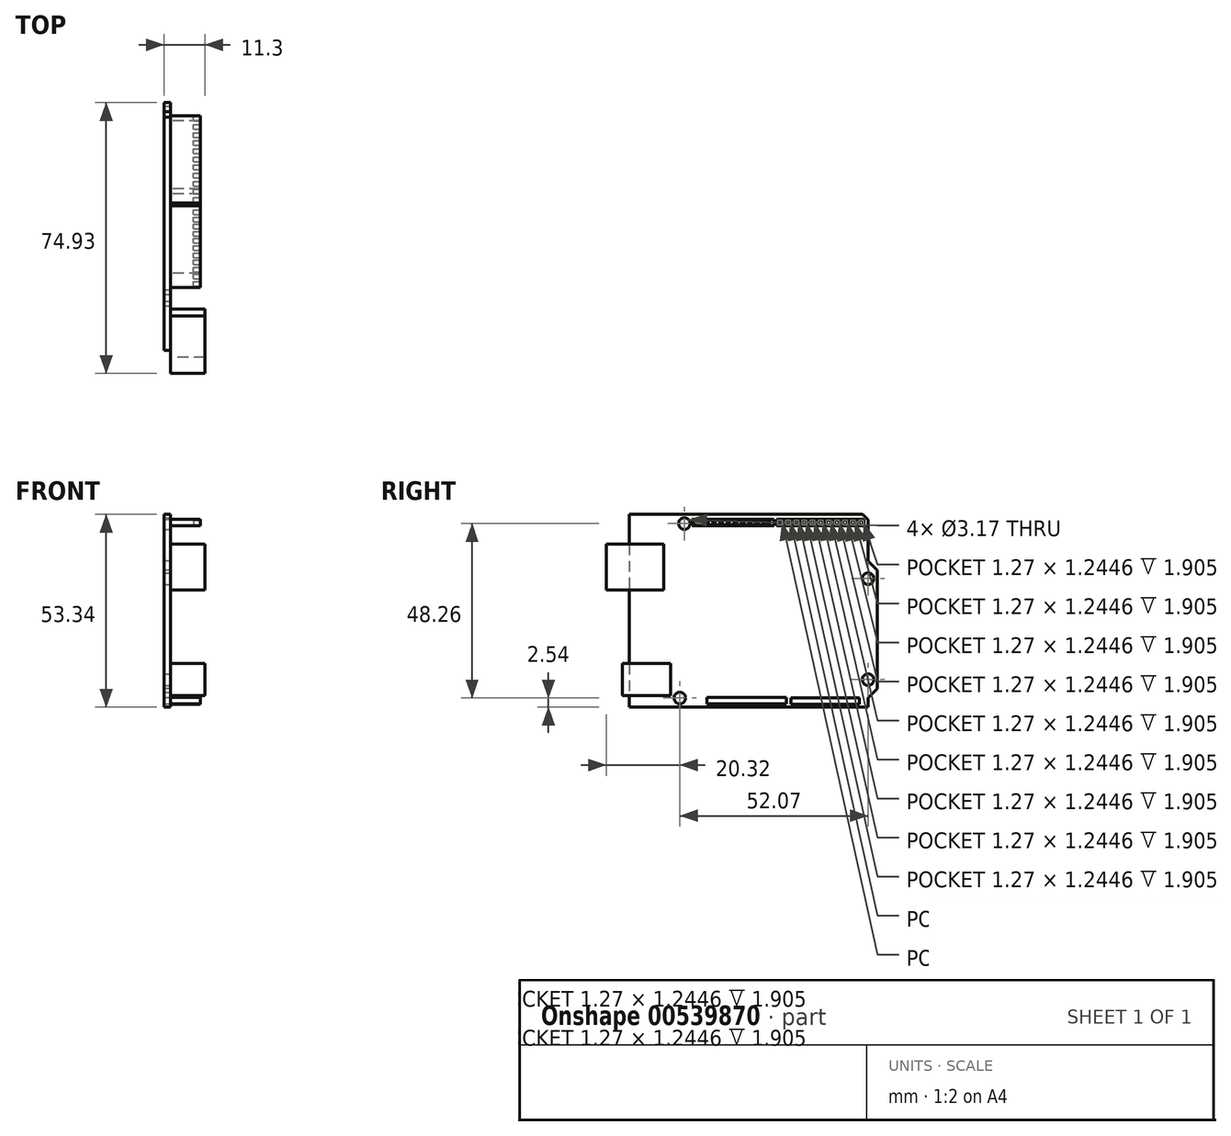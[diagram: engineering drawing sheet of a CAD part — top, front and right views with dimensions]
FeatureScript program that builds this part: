
annotation { "Feature Type Name" : "Feature", "Feature Type Description" : "" }
export const myFeature = defineFeature(function(context is Context, id is Id, definition is map)
    precondition{}
    {
        {
            var Q0;
            Q0=qCreatedBy(makeId("Right.planeOp"),FACE);
            var sketch = newSketch(context, id + "F0", { "sketchPlane" : qUnion([Q0])});
            skPoint(sketch, "E0", {"position": v(0, 53.34) * mm});
            skPoint(sketch, "E1", {"position": v(64.52, 53.34) * mm});
            skPoint(sketch, "E2", {"position": v(66.04, 0) * mm});
            skPoint(sketch, "E3", {"position": v(66.04, 2.54) * mm});
            skPoint(sketch, "E4", {"position": v(68.58, 5.08) * mm});
            skPoint(sketch, "E5", {"position": v(68.58, 37.85) * mm});
            skPoint(sketch, "E6", {"position": v(66.04, 40.39) * mm});
            skPoint(sketch, "E7", {"position": v(66.04, 51.82) * mm});
            skLineSegment(sketch, "E8", {"start": v(0, 53.34) * mm, "end": v(0, 0) * mm});
            skLineSegment(sketch, "E9", {"start": v(0, 0) * mm, "end": v(66.04, 0) * mm});
            skLineSegment(sketch, "E10", {"start": v(66.04, 2.54) * mm, "end": v(68.58, 5.08) * mm});
            skLineSegment(sketch, "E11", {"start": v(68.58, 37.85) * mm, "end": v(66.04, 40.39) * mm});
            skLineSegment(sketch, "E12", {"start": v(66.04, 51.82) * mm, "end": v(64.52, 53.34) * mm});
            skLineSegment(sketch, "E13", {"start": v(66.04, 2.54) * mm, "end": v(66.04, 0) * mm});
            skLineSegment(sketch, "E14", {"start": v(68.58, 5.08) * mm, "end": v(68.58, 37.85) * mm});
            skLineSegment(sketch, "E15", {"start": v(66.04, 40.39) * mm, "end": v(66.04, 51.82) * mm});
            skLineSegment(sketch, "E16", {"start": v(0, 53.34) * mm, "end": v(64.52, 53.34) * mm});
            skSolve(sketch);
        }
        {
            var Q0;
            Q0 = qSketchRegion(id + "F0", true);
            extrude(context, id + "F1", {"entities" : qUnion([Q0]), "depth" : 1.78 * mm, "offsetDistance" : 25.4 * mm});
        }
        {
            var Q0;
            Q0=makeQuery(id+"F1.opExtrude","CAP_FACE",FACE,{"disambiguationData":[OSD([sQuery(id+"F0.wireOp",EDGE,"E10"),sQuery(id+"F0.wireOp",EDGE,"E11"),sQuery(id+"F0.wireOp",EDGE,"E12"),sQuery(id+"F0.wireOp",EDGE,"E9"),sQuery(id+"F0.wireOp",EDGE,"E13"),sQuery(id+"F0.wireOp",EDGE,"E14"),sQuery(id+"F0.wireOp",EDGE,"E15"),sQuery(id+"F0.wireOp",EDGE,"E16"),sQuery(id+"F0.wireOp",EDGE,"E8")])],"isStart":false});
            var sketch = newSketch(context, id + "F2", { "sketchPlane" : qUnion([Q0])});
            skCircle(sketch, "E17", {"center": v(13.97, 2.54) * mm, "radius": 1.59 * mm});
            skCircle(sketch, "E18", {"center": v(15.24, 50.8) * mm, "radius": 1.59 * mm});
            skCircle(sketch, "E19", {"center": v(66.04, 35.56) * mm, "radius": 1.59 * mm});
            skCircle(sketch, "E20", {"center": v(66.04, 7.62) * mm, "radius": 1.59 * mm});
            skSolve(sketch);
        }
        {
            var Q0;
            Q0 = qSketchRegion(id + "F2", true);
            extrude(context, id + "F3", {"entities" : qUnion([Q0]), "operationType" : NewBodyOperationType.REMOVE, "oppositeDirection" : true, "depth" : 1.78 * mm, "offsetDistance" : 25.4 * mm});
        }
        {
            var Q0;
            Q0=makeQuery(id+"F1.opExtrude","CAP_FACE",FACE,{"disambiguationData":[OSD([sQuery(id+"F0.wireOp",EDGE,"E10"),sQuery(id+"F0.wireOp",EDGE,"E11"),sQuery(id+"F0.wireOp",EDGE,"E12"),sQuery(id+"F0.wireOp",EDGE,"E9"),sQuery(id+"F0.wireOp",EDGE,"E13"),sQuery(id+"F0.wireOp",EDGE,"E14"),sQuery(id+"F0.wireOp",EDGE,"E15"),sQuery(id+"F0.wireOp",EDGE,"E16"),sQuery(id+"F0.wireOp",EDGE,"E8")])],"isStart":false});
            var sketch = newSketch(context, id + "F4", { "sketchPlane" : qUnion([Q0])});
            skLineSegment(sketch, "E21.bottom", {"start": v(-1.9, 12.07) * mm, "end": v(11.43, 12.07) * mm});
            skLineSegment(sketch, "E21.top", {"start": v(-1.9, 3.18) * mm, "end": v(11.43, 3.18) * mm});
            skLineSegment(sketch, "E21.left", {"start": v(-1.9, 12.06) * mm, "end": v(-1.9, 3.17) * mm});
            skLineSegment(sketch, "E21.right", {"start": v(11.43, 12.07) * mm, "end": v(11.43, 3.18) * mm});
            skLineSegment(sketch, "E22.bottom", {"start": v(-6.35, 45.09) * mm, "end": v(9.53, 45.09) * mm});
            skLineSegment(sketch, "E22.top", {"start": v(-6.35, 32.39) * mm, "end": v(9.53, 32.39) * mm});
            skLineSegment(sketch, "E22.left", {"start": v(-6.35, 45.09) * mm, "end": v(-6.35, 32.39) * mm});
            skLineSegment(sketch, "E22.right", {"start": v(9.53, 45.09) * mm, "end": v(9.53, 32.39) * mm});
            skSolve(sketch);
        }
        {
            var Q0;
            Q0 = qSketchRegion(id + "F4", true);
            extrude(context, id + "F5", {"entities" : qUnion([Q0]), "depth" : 9.52 * mm, "offsetDistance" : 25.4 * mm});
        }
        {
            var Q0;
            Q0=makeQuery(id+"F1.opExtrude","CAP_FACE",FACE,{"disambiguationData":[OSD([sQuery(id+"F0.wireOp",EDGE,"E10"),sQuery(id+"F0.wireOp",EDGE,"E11"),sQuery(id+"F0.wireOp",EDGE,"E12"),sQuery(id+"F0.wireOp",EDGE,"E9"),sQuery(id+"F0.wireOp",EDGE,"E13"),sQuery(id+"F0.wireOp",EDGE,"E14"),sQuery(id+"F0.wireOp",EDGE,"E15"),sQuery(id+"F0.wireOp",EDGE,"E16"),sQuery(id+"F0.wireOp",EDGE,"E8")])],"isStart":false});
            var sketch = newSketch(context, id + "F6", { "sketchPlane" : qUnion([Q0])});
            skLineSegment(sketch, "E23.bottom", {"start": v(17.39, 52.02) * mm, "end": v(39.99, 52.02) * mm});
            skLineSegment(sketch, "E23.top", {"start": v(17.39, 50.24) * mm, "end": v(39.99, 50.24) * mm});
            skLineSegment(sketch, "E23.left", {"start": v(17.39, 52.02) * mm, "end": v(17.39, 50.24) * mm});
            skLineSegment(sketch, "E23.right", {"start": v(39.99, 52.02) * mm, "end": v(39.99, 50.24) * mm});
            skLineSegment(sketch, "E24.bottom", {"start": v(40.75, 52.02) * mm, "end": v(64.96, 52.02) * mm});
            skLineSegment(sketch, "E24.top", {"start": v(40.75, 50.24) * mm, "end": v(64.96, 50.24) * mm});
            skLineSegment(sketch, "E24.left", {"start": v(40.75, 52.02) * mm, "end": v(40.75, 50.24) * mm});
            skLineSegment(sketch, "E24.right", {"start": v(64.96, 52.02) * mm, "end": v(64.96, 50.24) * mm});
            skLineSegment(sketch, "E25.bottom", {"start": v(21.43, 0.92) * mm, "end": v(43.38, 0.92) * mm});
            skLineSegment(sketch, "E25.top", {"start": v(21.43, 2.7) * mm, "end": v(43.38, 2.7) * mm});
            skLineSegment(sketch, "E25.left", {"start": v(21.43, 0.92) * mm, "end": v(21.43, 2.7) * mm});
            skLineSegment(sketch, "E25.right", {"start": v(43.38, 0.92) * mm, "end": v(43.38, 2.7) * mm});
            skLineSegment(sketch, "E26.bottom", {"start": v(44.71, 2.62) * mm, "end": v(63.57, 2.62) * mm});
            skLineSegment(sketch, "E26.top", {"start": v(44.71, 0.84) * mm, "end": v(63.57, 0.84) * mm});
            skLineSegment(sketch, "E26.left", {"start": v(44.71, 2.62) * mm, "end": v(44.71, 0.84) * mm});
            skLineSegment(sketch, "E26.right", {"start": v(63.57, 2.62) * mm, "end": v(63.57, 0.84) * mm});
            skSolve(sketch);
        }
        {
            var Q0;
            Q0 = qSketchRegion(id + "F6", true);
            extrude(context, id + "F7", {"entities" : qUnion([Q0]), "depth" : 8.25 * mm, "offsetDistance" : 25.4 * mm});
        }
        {
            var Q0;
            Q0=makeQuery(id+"F7.opExtrude","CAP_FACE",FACE,{"disambiguationData":[OSD([sQuery(id+"F6.wireOp",EDGE,"E23.bottom"),sQuery(id+"F6.wireOp",EDGE,"E23.top"),sQuery(id+"F6.wireOp",EDGE,"E23.left"),sQuery(id+"F6.wireOp",EDGE,"E23.right")])],"isStart":false});
            var sketch = newSketch(context, id + "F8", { "sketchPlane" : qUnion([Q0])});
            skLineSegment(sketch, "E27.bottom", {"start": v(17.83, 51.76) * mm, "end": v(19.1, 51.76) * mm});
            skLineSegment(sketch, "E27.top", {"start": v(17.83, 50.53) * mm, "end": v(19.1, 50.53) * mm});
            skLineSegment(sketch, "E27.left", {"start": v(17.83, 51.76) * mm, "end": v(17.83, 50.53) * mm});
            skLineSegment(sketch, "E27.right", {"start": v(19.1, 51.76) * mm, "end": v(19.1, 50.53) * mm});
            skLineSegment(sketch, "E28.1.0.0", {"start": v(19.8, 51.76) * mm, "end": v(19.8, 50.53) * mm});
            skLineSegment(sketch, "E28.1.0.1", {"start": v(19.8, 51.76) * mm, "end": v(21.08, 51.76) * mm});
            skLineSegment(sketch, "E28.1.0.2", {"start": v(21.08, 51.76) * mm, "end": v(21.08, 50.53) * mm});
            skLineSegment(sketch, "E28.1.0.3", {"start": v(19.8, 50.53) * mm, "end": v(21.08, 50.53) * mm});
            skLineSegment(sketch, "E28.2.0.0", {"start": v(21.8, 51.76) * mm, "end": v(21.8, 50.53) * mm});
            skLineSegment(sketch, "E28.2.0.1", {"start": v(21.8, 51.76) * mm, "end": v(23.06, 51.76) * mm});
            skLineSegment(sketch, "E28.2.0.2", {"start": v(23.06, 51.76) * mm, "end": v(23.06, 50.53) * mm});
            skLineSegment(sketch, "E28.2.0.3", {"start": v(21.8, 50.53) * mm, "end": v(23.06, 50.53) * mm});
            skLineSegment(sketch, "E28.3.0.0", {"start": v(23.77, 51.76) * mm, "end": v(23.77, 50.53) * mm});
            skLineSegment(sketch, "E28.3.0.1", {"start": v(23.77, 51.76) * mm, "end": v(25.04, 51.76) * mm});
            skLineSegment(sketch, "E28.3.0.2", {"start": v(25.04, 51.76) * mm, "end": v(25.04, 50.53) * mm});
            skLineSegment(sketch, "E28.3.0.3", {"start": v(23.77, 50.53) * mm, "end": v(25.04, 50.53) * mm});
            skLineSegment(sketch, "E28.4.0.0", {"start": v(25.75, 51.76) * mm, "end": v(25.75, 50.53) * mm});
            skLineSegment(sketch, "E28.4.0.1", {"start": v(25.75, 51.76) * mm, "end": v(27.02, 51.76) * mm});
            skLineSegment(sketch, "E28.4.0.2", {"start": v(27.02, 51.76) * mm, "end": v(27.02, 50.53) * mm});
            skLineSegment(sketch, "E28.4.0.3", {"start": v(25.75, 50.53) * mm, "end": v(27.02, 50.53) * mm});
            skLineSegment(sketch, "E28.5.0.0", {"start": v(27.73, 51.76) * mm, "end": v(27.73, 50.53) * mm});
            skLineSegment(sketch, "E28.5.0.1", {"start": v(27.73, 51.76) * mm, "end": v(29, 51.76) * mm});
            skLineSegment(sketch, "E28.5.0.2", {"start": v(29, 51.76) * mm, "end": v(29, 50.53) * mm});
            skLineSegment(sketch, "E28.5.0.3", {"start": v(27.73, 50.53) * mm, "end": v(29, 50.53) * mm});
            skLineSegment(sketch, "E28.6.0.0", {"start": v(29.72, 51.76) * mm, "end": v(29.72, 50.53) * mm});
            skLineSegment(sketch, "E28.6.0.1", {"start": v(29.72, 51.76) * mm, "end": v(30.98, 51.76) * mm});
            skLineSegment(sketch, "E28.6.0.2", {"start": v(30.98, 51.76) * mm, "end": v(30.98, 50.53) * mm});
            skLineSegment(sketch, "E28.6.0.3", {"start": v(29.72, 50.53) * mm, "end": v(30.98, 50.53) * mm});
            skLineSegment(sketch, "E28.7.0.0", {"start": v(31.7, 51.76) * mm, "end": v(31.7, 50.53) * mm});
            skLineSegment(sketch, "E28.7.0.1", {"start": v(31.7, 51.76) * mm, "end": v(32.97, 51.76) * mm});
            skLineSegment(sketch, "E28.7.0.2", {"start": v(32.97, 51.76) * mm, "end": v(32.97, 50.53) * mm});
            skLineSegment(sketch, "E28.7.0.3", {"start": v(31.7, 50.53) * mm, "end": v(32.97, 50.53) * mm});
            skLineSegment(sketch, "E28.8.0.0", {"start": v(33.68, 51.76) * mm, "end": v(33.68, 50.53) * mm});
            skLineSegment(sketch, "E28.8.0.1", {"start": v(33.68, 51.76) * mm, "end": v(34.95, 51.76) * mm});
            skLineSegment(sketch, "E28.8.0.2", {"start": v(34.95, 51.76) * mm, "end": v(34.95, 50.53) * mm});
            skLineSegment(sketch, "E28.8.0.3", {"start": v(33.68, 50.53) * mm, "end": v(34.95, 50.53) * mm});
            skLineSegment(sketch, "E28.9.0.0", {"start": v(35.66, 51.76) * mm, "end": v(35.66, 50.53) * mm});
            skLineSegment(sketch, "E28.9.0.1", {"start": v(35.66, 51.76) * mm, "end": v(36.93, 51.76) * mm});
            skLineSegment(sketch, "E28.9.0.2", {"start": v(36.93, 51.76) * mm, "end": v(36.93, 50.53) * mm});
            skLineSegment(sketch, "E28.9.0.3", {"start": v(35.66, 50.53) * mm, "end": v(36.93, 50.53) * mm});
            skLineSegment(sketch, "E28.10.0.0", {"start": v(37.64, 51.76) * mm, "end": v(37.64, 50.53) * mm});
            skLineSegment(sketch, "E28.10.0.1", {"start": v(37.64, 51.76) * mm, "end": v(38.9, 51.76) * mm});
            skLineSegment(sketch, "E28.10.0.2", {"start": v(38.9, 51.76) * mm, "end": v(38.9, 50.53) * mm});
            skLineSegment(sketch, "E28.10.0.3", {"start": v(37.64, 50.53) * mm, "end": v(38.9, 50.53) * mm});
            skLineSegment(sketch, "E28.direction1", {"start": v(17.83, 50.53) * mm, "end": v(19.8, 50.53) * mm, "construction": true});
            skLineSegment(sketch, "E29.bottom", {"start": v(41.06, 51.77) * mm, "end": v(42.33, 51.77) * mm});
            skLineSegment(sketch, "E29.top", {"start": v(41.06, 50.53) * mm, "end": v(42.33, 50.53) * mm});
            skLineSegment(sketch, "E29.left", {"start": v(41.06, 51.77) * mm, "end": v(41.06, 50.53) * mm});
            skLineSegment(sketch, "E29.right", {"start": v(42.33, 51.77) * mm, "end": v(42.33, 50.53) * mm});
            skLineSegment(sketch, "E30.1.0.0", {"start": v(44.58, 51.77) * mm, "end": v(44.58, 50.52) * mm});
            skLineSegment(sketch, "E30.1.0.1", {"start": v(43.3, 51.77) * mm, "end": v(44.58, 51.77) * mm});
            skLineSegment(sketch, "E30.1.0.2", {"start": v(43.3, 51.77) * mm, "end": v(43.3, 50.52) * mm});
            skLineSegment(sketch, "E30.1.0.3", {"start": v(43.3, 50.52) * mm, "end": v(44.58, 50.52) * mm});
            skLineSegment(sketch, "E30.2.0.0", {"start": v(46.82, 51.76) * mm, "end": v(46.82, 50.51) * mm});
            skLineSegment(sketch, "E30.2.0.1", {"start": v(45.55, 51.76) * mm, "end": v(46.82, 51.76) * mm});
            skLineSegment(sketch, "E30.2.0.2", {"start": v(45.55, 51.76) * mm, "end": v(45.55, 50.51) * mm});
            skLineSegment(sketch, "E30.2.0.3", {"start": v(45.55, 50.51) * mm, "end": v(46.82, 50.51) * mm});
            skLineSegment(sketch, "E30.3.0.0", {"start": v(49.06, 51.75) * mm, "end": v(49.06, 50.5) * mm});
            skLineSegment(sketch, "E30.3.0.1", {"start": v(47.8, 51.75) * mm, "end": v(49.06, 51.75) * mm});
            skLineSegment(sketch, "E30.3.0.2", {"start": v(47.8, 51.75) * mm, "end": v(47.8, 50.5) * mm});
            skLineSegment(sketch, "E30.3.0.3", {"start": v(47.8, 50.5) * mm, "end": v(49.06, 50.5) * mm});
            skLineSegment(sketch, "E30.4.0.0", {"start": v(51.3, 51.74) * mm, "end": v(51.3, 50.5) * mm});
            skLineSegment(sketch, "E30.4.0.1", {"start": v(50.03, 51.74) * mm, "end": v(51.3, 51.74) * mm});
            skLineSegment(sketch, "E30.4.0.2", {"start": v(50.03, 51.74) * mm, "end": v(50.03, 50.5) * mm});
            skLineSegment(sketch, "E30.4.0.3", {"start": v(50.03, 50.5) * mm, "end": v(51.3, 50.5) * mm});
            skLineSegment(sketch, "E30.5.0.0", {"start": v(53.55, 51.73) * mm, "end": v(53.55, 50.49) * mm});
            skLineSegment(sketch, "E30.5.0.1", {"start": v(52.28, 51.73) * mm, "end": v(53.55, 51.73) * mm});
            skLineSegment(sketch, "E30.5.0.2", {"start": v(52.28, 51.73) * mm, "end": v(52.28, 50.49) * mm});
            skLineSegment(sketch, "E30.5.0.3", {"start": v(52.28, 50.49) * mm, "end": v(53.55, 50.49) * mm});
            skLineSegment(sketch, "E30.6.0.0", {"start": v(55.79, 51.73) * mm, "end": v(55.79, 50.48) * mm});
            skLineSegment(sketch, "E30.6.0.1", {"start": v(54.52, 51.73) * mm, "end": v(55.79, 51.73) * mm});
            skLineSegment(sketch, "E30.6.0.2", {"start": v(54.52, 51.73) * mm, "end": v(54.52, 50.48) * mm});
            skLineSegment(sketch, "E30.6.0.3", {"start": v(54.52, 50.48) * mm, "end": v(55.79, 50.48) * mm});
            skLineSegment(sketch, "E30.7.0.0", {"start": v(58.03, 51.72) * mm, "end": v(58.03, 50.47) * mm});
            skLineSegment(sketch, "E30.7.0.1", {"start": v(56.76, 51.72) * mm, "end": v(58.03, 51.72) * mm});
            skLineSegment(sketch, "E30.7.0.2", {"start": v(56.76, 51.72) * mm, "end": v(56.76, 50.47) * mm});
            skLineSegment(sketch, "E30.7.0.3", {"start": v(56.76, 50.47) * mm, "end": v(58.03, 50.47) * mm});
            skLineSegment(sketch, "E30.8.0.0", {"start": v(60.27, 51.7) * mm, "end": v(60.27, 50.46) * mm});
            skLineSegment(sketch, "E30.8.0.1", {"start": v(59, 51.7) * mm, "end": v(60.27, 51.7) * mm});
            skLineSegment(sketch, "E30.8.0.2", {"start": v(59, 51.7) * mm, "end": v(59, 50.46) * mm});
            skLineSegment(sketch, "E30.8.0.3", {"start": v(59, 50.46) * mm, "end": v(60.27, 50.46) * mm});
            skLineSegment(sketch, "E30.9.0.0", {"start": v(62.52, 51.7) * mm, "end": v(62.52, 50.46) * mm});
            skLineSegment(sketch, "E30.9.0.1", {"start": v(61.25, 51.7) * mm, "end": v(62.52, 51.7) * mm});
            skLineSegment(sketch, "E30.9.0.2", {"start": v(61.25, 51.7) * mm, "end": v(61.25, 50.46) * mm});
            skLineSegment(sketch, "E30.9.0.3", {"start": v(61.25, 50.46) * mm, "end": v(62.52, 50.46) * mm});
            skLineSegment(sketch, "E30.10.0.0", {"start": v(64.76, 51.7) * mm, "end": v(64.76, 50.45) * mm});
            skLineSegment(sketch, "E30.10.0.1", {"start": v(63.49, 51.7) * mm, "end": v(64.76, 51.7) * mm});
            skLineSegment(sketch, "E30.10.0.2", {"start": v(63.49, 51.7) * mm, "end": v(63.49, 50.45) * mm});
            skLineSegment(sketch, "E30.10.0.3", {"start": v(63.49, 50.45) * mm, "end": v(64.76, 50.45) * mm});
            skLineSegment(sketch, "E30.direction1", {"start": v(42.33, 50.53) * mm, "end": v(44.58, 50.52) * mm, "construction": true});
            skSolve(sketch);
        }
        {
            var Q0;
            Q0 = qSketchRegion(id + "F8", true);
            extrude(context, id + "F9", {"entities" : qUnion([Q0]), "operationType" : NewBodyOperationType.REMOVE, "oppositeDirection" : true, "depth" : 1.9 * mm, "offsetDistance" : 25.4 * mm});
        }
    });
